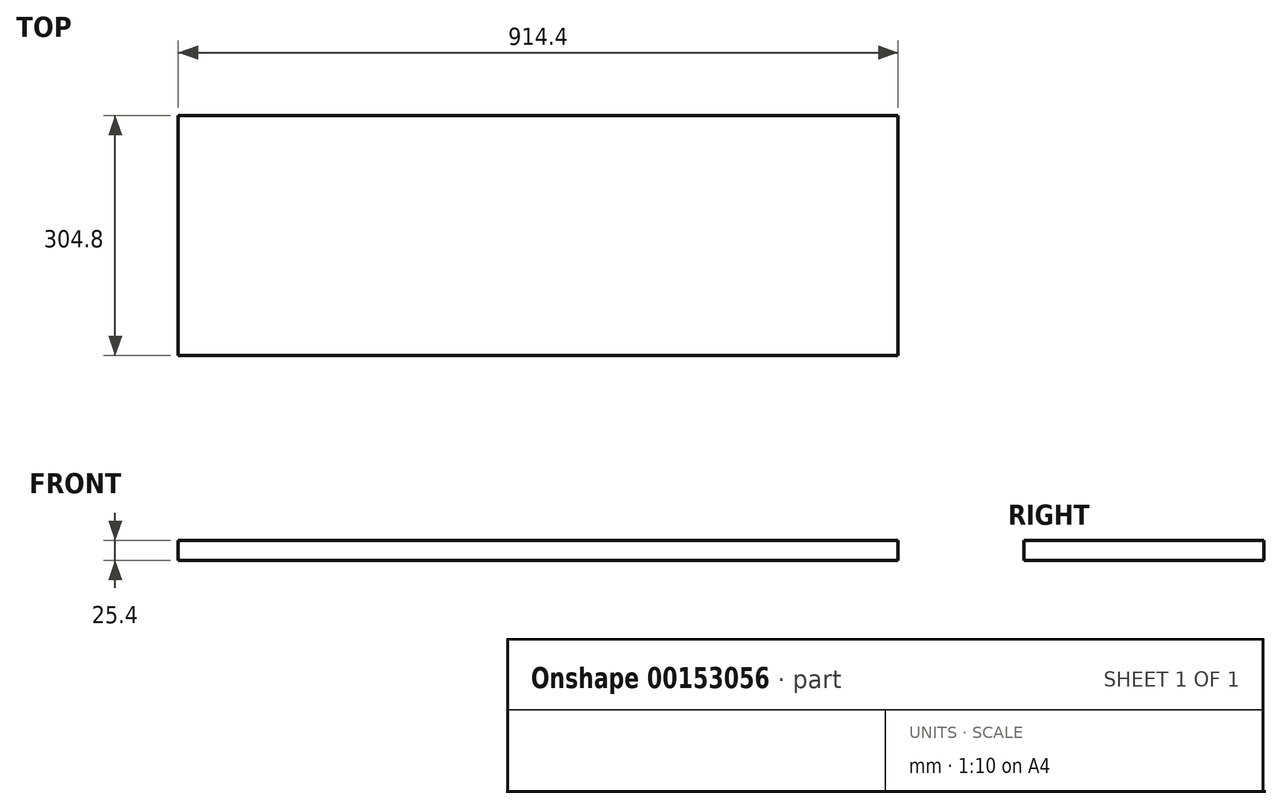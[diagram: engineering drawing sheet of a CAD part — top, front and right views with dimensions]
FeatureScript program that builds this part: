
annotation { "Feature Type Name" : "Feature", "Feature Type Description" : "" }
export const myFeature = defineFeature(function(context is Context, id is Id, definition is map)
    precondition{}
    {
        {
            var Q0;
            Q0=qCreatedBy(makeId("Top.planeOp"),FACE);
            var sketch = newSketch(context, id + "F0", { "sketchPlane" : qUnion([Q0])});
            skLineSegment(sketch, "E0.bottom", {"start": v(0, 0) * mm, "end": v(914.4, 0) * mm});
            skLineSegment(sketch, "E0.top", {"start": v(0, 304.8) * mm, "end": v(914.4, 304.8) * mm});
            skLineSegment(sketch, "E0.left", {"start": v(0, 0) * mm, "end": v(0, 304.8) * mm});
            skLineSegment(sketch, "E0.right", {"start": v(914.4, 0) * mm, "end": v(914.4, 304.8) * mm});
            skSolve(sketch);
        }
        {
            var Q0;
            Q0=makeQuery(id+"F0.imprint","IMPRINT",FACE,{"disambiguationData":[TD([[makeQuery(id+"F0.imprint","IMPRINT",EDGE,{"derivedFrom":sQuery(id+"F0.wireOp",EDGE,"E0.bottom")}),1.0]])]});
            extrude(context, id + "F1", {"entities" : qUnion([Q0]), "depth" : 25.4 * mm});
        }
    });
